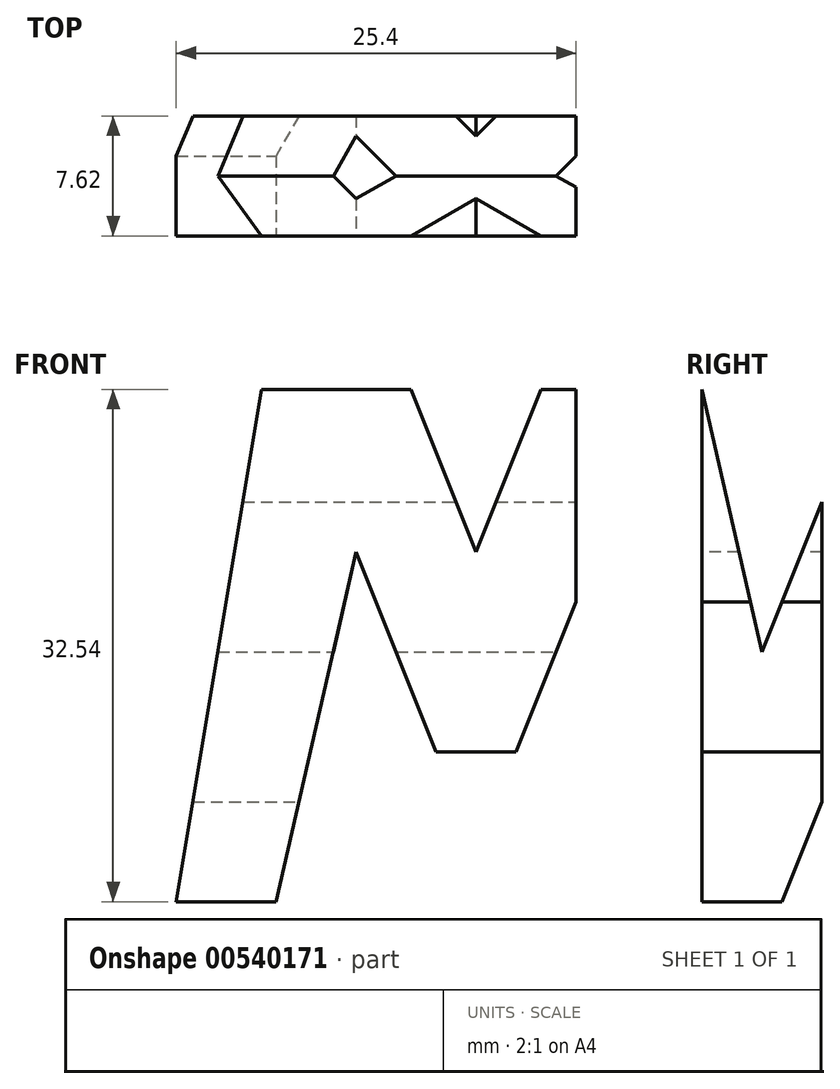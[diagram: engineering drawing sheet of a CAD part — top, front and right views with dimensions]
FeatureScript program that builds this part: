
annotation { "Feature Type Name" : "Feature", "Feature Type Description" : "" }
export const myFeature = defineFeature(function(context is Context, id is Id, definition is map)
    precondition{}
    {
        {
            var Q0;
            Q0=qCreatedBy(makeId("Front.planeOp"),FACE);
            var sketch = newSketch(context, id + "F0", { "sketchPlane" : qUnion([Q0])});
            skLineSegment(sketch, "E0", {"start": v(0, 0) * mm, "end": v(0, 38.1) * mm});
            skLineSegment(sketch, "E1", {"start": v(0, 38.1) * mm, "end": v(38.1, 38.1) * mm});
            skLineSegment(sketch, "E2", {"start": v(38.1, 38.1) * mm, "end": v(38.1, 0) * mm});
            skLineSegment(sketch, "E3", {"start": v(38.1, 0) * mm, "end": v(0, 0) * mm});
            skSolve(sketch);
        }
        {
            var Q0;
            Q0 = qSketchRegion(id + "F0", true);
            extrude(context, id + "F1", {"entities" : qUnion([Q0]), "depth" : 38.1 * mm, "offsetDistance" : 25.4 * mm});
        }
        {
            var Q0;
            Q0=qCreatedBy(makeId("Front.planeOp"),FACE);
            cPlane(context, id + "F2", {"entities" : qUnion([Q0]), "cplaneType" : CPlaneType.OFFSET, "offset" : 38.1 * mm, "width" : 152.4 * mm, "height" : 152.4 * mm});
        }
        {
            var Q0;
            Q0=qCreatedBy(makeId("Right.planeOp"),FACE);
            cPlane(context, id + "F3", {"entities" : qUnion([Q0]), "cplaneType" : CPlaneType.OFFSET, "offset" : 38.1 * mm, "width" : 152.4 * mm, "height" : 152.4 * mm});
        }
        {
            var Q0;
            Q0=qCreatedBy(makeId("Top.planeOp"),FACE);
            cPlane(context, id + "F4", {"entities" : qUnion([Q0]), "cplaneType" : CPlaneType.OFFSET, "offset" : 38.1 * mm, "width" : 152.4 * mm, "height" : 152.4 * mm});
        }
        {
            var Q0;
            Q0=qCreatedBy(id+"F3.planeOp",FACE);
            var sketch = newSketch(context, id + "F5", { "sketchPlane" : qUnion([Q0])});
            skLineSegment(sketch, "E4", {"start": v(0, 0) * mm, "end": v(0, 38.1) * mm});
            skLineSegment(sketch, "E5", {"start": v(0, 38.1) * mm, "end": v(-38.1, 38.1) * mm});
            skLineSegment(sketch, "E6", {"start": v(-38.1, 38.1) * mm, "end": v(-38.1, 0) * mm});
            skLineSegment(sketch, "E7", {"start": v(-38.1, 0) * mm, "end": v(0, 0) * mm});
            skLineSegment(sketch, "E8", {"start": v(-38.1, 38.1) * mm, "end": v(-31.75, 0) * mm});
            skLineSegment(sketch, "E9", {"start": v(-31.75, 0) * mm, "end": v(-25.4, 0) * mm});
            skLineSegment(sketch, "E10", {"start": v(-25.4, 0) * mm, "end": v(-19.05, 15.87) * mm});
            skLineSegment(sketch, "E11", {"start": v(-19.05, 15.87) * mm, "end": v(-12.7, 0) * mm});
            skLineSegment(sketch, "E12", {"start": v(-12.7, 0) * mm, "end": v(-6.35, 0) * mm});
            skLineSegment(sketch, "E13", {"start": v(-6.35, 0) * mm, "end": v(0, 38.1) * mm});
            skLineSegment(sketch, "E14", {"start": v(-6.35, 38.1) * mm, "end": v(-11.43, 15.87) * mm});
            skLineSegment(sketch, "E15", {"start": v(-11.43, 15.87) * mm, "end": v(-16.5, 28.57) * mm});
            skLineSegment(sketch, "E16", {"start": v(-16.5, 28.57) * mm, "end": v(-21.59, 28.57) * mm});
            skLineSegment(sketch, "E17", {"start": v(-31.75, 38.1) * mm, "end": v(-38.1, 38.1) * mm});
            skLineSegment(sketch, "E18", {"start": v(-31.75, 38.1) * mm, "end": v(-26.67, 15.87) * mm});
            skLineSegment(sketch, "E19", {"start": v(-26.67, 15.87) * mm, "end": v(-21.59, 28.57) * mm});
            skSolve(sketch);
        }
        {
            var Q0;
            {var subQ0=sQuery(id+"F5.wireOp",EDGE,"E14");Q0=makeQuery(id+"F5.imprint","IMPRINT",FACE,{"disambiguationData":[TD([[makeQuery(id+"F5.imprint","IMPRINT",EDGE,{"derivedFrom":subQ0}),-1.0]])]});}
            var Q1;
            {var subQ0=sQuery(id+"F5.wireOp",EDGE,"E6");Q1=makeQuery(id+"F5.imprint","IMPRINT",FACE,{"disambiguationData":[TD([[makeQuery(id+"F5.imprint","IMPRINT",EDGE,{"derivedFrom":subQ0}),1.0]])]});}
            var Q2;
            {var subQ0=sQuery(id+"F5.wireOp",EDGE,"E10");Q2=makeQuery(id+"F5.imprint","IMPRINT",FACE,{"disambiguationData":[TD([[makeQuery(id+"F5.imprint","IMPRINT",EDGE,{"derivedFrom":subQ0}),-1.0]])]});}
            var Q3;
            {var subQ0=sQuery(id+"F5.wireOp",EDGE,"E4");Q3=makeQuery(id+"F5.imprint","IMPRINT",FACE,{"disambiguationData":[TD([[makeQuery(id+"F5.imprint","IMPRINT",EDGE,{"derivedFrom":subQ0}),1.0]])]});}
            extrude(context, id + "F6", {"entities" : qUnion([Q0, Q1, Q2, Q3]), "operationType" : NewBodyOperationType.REMOVE, "oppositeDirection" : true, "depth" : 38.1 * mm, "offsetDistance" : 25.4 * mm});
        }
        {
            var Q0;
            Q0=qCreatedBy(id+"F2.planeOp",FACE);
            var sketch = newSketch(context, id + "F7", { "sketchPlane" : qUnion([Q0])});
            skLineSegment(sketch, "E20", {"start": v(0, 0) * mm, "end": v(0, 38.1) * mm});
            skLineSegment(sketch, "E21", {"start": v(0, 38.1) * mm, "end": v(38.1, 38.1) * mm});
            skLineSegment(sketch, "E22", {"start": v(38.1, 38.1) * mm, "end": v(38.1, 0) * mm});
            skLineSegment(sketch, "E23", {"start": v(38.1, 0) * mm, "end": v(0, 0) * mm});
            skLineSegment(sketch, "E24", {"start": v(38.1, 0) * mm, "end": v(31.75, 38.1) * mm});
            skLineSegment(sketch, "E25", {"start": v(31.75, 38.1) * mm, "end": v(25.4, 38.1) * mm});
            skLineSegment(sketch, "E26", {"start": v(25.4, 38.1) * mm, "end": v(19.05, 22.22) * mm});
            skLineSegment(sketch, "E27", {"start": v(19.05, 22.23) * mm, "end": v(12.7, 38.1) * mm});
            skLineSegment(sketch, "E28", {"start": v(12.7, 38.1) * mm, "end": v(6.35, 38.1) * mm});
            skPoint(sketch, "E29.end.orphan", {"position": v(0, -1.28) * mm});
            skLineSegment(sketch, "E30", {"start": v(6.35, 38.1) * mm, "end": v(0, 0) * mm});
            skLineSegment(sketch, "E31", {"start": v(6.35, 0) * mm, "end": v(11.43, 22.23) * mm});
            skLineSegment(sketch, "E32", {"start": v(11.43, 22.23) * mm, "end": v(16.51, 9.53) * mm});
            skLineSegment(sketch, "E33", {"start": v(16.51, 9.53) * mm, "end": v(21.59, 9.53) * mm});
            skLineSegment(sketch, "E34", {"start": v(21.59, 9.53) * mm, "end": v(26.67, 22.23) * mm});
            skLineSegment(sketch, "E35", {"start": v(26.67, 22.23) * mm, "end": v(31.75, 0) * mm});
            skLineSegment(sketch, "E36", {"start": v(31.75, 0) * mm, "end": v(38.1, 0) * mm});
            skSolve(sketch);
        }
        {
            var Q0;
            {var subQ0=sQuery(id+"F7.wireOp",EDGE,"E20");Q0=makeQuery(id+"F7.imprint","IMPRINT",FACE,{"disambiguationData":[TD([[makeQuery(id+"F7.imprint","IMPRINT",EDGE,{"derivedFrom":subQ0}),-1.0]])]});}
            var Q1;
            {var subQ0=sQuery(id+"F7.wireOp",EDGE,"E26");Q1=makeQuery(id+"F7.imprint","IMPRINT",FACE,{"disambiguationData":[TD([[makeQuery(id+"F7.imprint","IMPRINT",EDGE,{"derivedFrom":subQ0}),-1.0]])]});}
            var Q2;
            {var subQ0=sQuery(id+"F7.wireOp",EDGE,"E22");Q2=makeQuery(id+"F7.imprint","IMPRINT",FACE,{"disambiguationData":[TD([[makeQuery(id+"F7.imprint","IMPRINT",EDGE,{"derivedFrom":subQ0}),-1.0]])]});}
            var Q3;
            {var subQ0=sQuery(id+"F7.wireOp",EDGE,"E31");Q3=makeQuery(id+"F7.imprint","IMPRINT",FACE,{"disambiguationData":[TD([[makeQuery(id+"F7.imprint","IMPRINT",EDGE,{"derivedFrom":subQ0}),-1.0]])]});}
            extrude(context, id + "F8", {"entities" : qUnion([Q0, Q1, Q2, Q3]), "operationType" : NewBodyOperationType.REMOVE, "oppositeDirection" : true, "depth" : 38.1 * mm, "offsetDistance" : 25.4 * mm});
        }
        {
            var Q0;
            Q0=qCreatedBy(id+"F4.planeOp",FACE);
            var sketch = newSketch(context, id + "F9", { "sketchPlane" : qUnion([Q0])});
            skLineSegment(sketch, "E37", {"start": v(0, 0) * mm, "end": v(38.1, 0) * mm});
            skLineSegment(sketch, "E38", {"start": v(38.1, 0) * mm, "end": v(38.1, -38.1) * mm});
            skLineSegment(sketch, "E39", {"start": v(38.1, -38.1) * mm, "end": v(0, -38.1) * mm});
            skLineSegment(sketch, "E40", {"start": v(0, -38.1) * mm, "end": v(0, 0) * mm});
            skLineSegment(sketch, "E41", {"start": v(38.1, -7.62) * mm, "end": v(12.7, -7.62) * mm});
            skLineSegment(sketch, "E42", {"start": v(12.7, -7.62) * mm, "end": v(12.7, -15.24) * mm});
            skLineSegment(sketch, "E43", {"start": v(12.7, -15.24) * mm, "end": v(38.1, -15.24) * mm});
            skLineSegment(sketch, "E44", {"start": v(38.1, -15.24) * mm, "end": v(38.1, -38.1) * mm});
            skLineSegment(sketch, "E45", {"start": v(0, -38.1) * mm, "end": v(0, -30.48) * mm});
            skLineSegment(sketch, "E46", {"start": v(0, -30.48) * mm, "end": v(25.4, -30.48) * mm});
            skLineSegment(sketch, "E47", {"start": v(25.4, -30.48) * mm, "end": v(25.4, -22.86) * mm});
            skLineSegment(sketch, "E48", {"start": v(25.4, -22.86) * mm, "end": v(0, -22.86) * mm});
            skLineSegment(sketch, "E49", {"start": v(0, -22.86) * mm, "end": v(0, 0) * mm});
            skSolve(sketch);
        }
        {
            var Q0;
            {var subQ2=sQuery(id+"F9.wireOp",EDGE,"E41");Q0=makeQuery(id+"F9.imprint","IMPRINT",FACE,{"disambiguationData":[TD([[makeQuery(id+"F9.imprint","IMPRINT",EDGE,{"derivedFrom":subQ2}),1.0]])]});}
            var Q1;
            Q1=makeQuery(id+"F9.imprint","IMPRINT",FACE,{"disambiguationData":[TD([[makeQuery(id+"F9.imprint","IMPRINT",EDGE,{"derivedFrom":sQuery(id+"F9.wireOp",EDGE,"E40")}),-1.0]])]});
            extrude(context, id + "F10", {"entities" : qUnion([Q0, Q1]), "operationType" : NewBodyOperationType.REMOVE, "oppositeDirection" : true, "depth" : 38.1 * mm, "offsetDistance" : 25.4 * mm});
        }
    });
